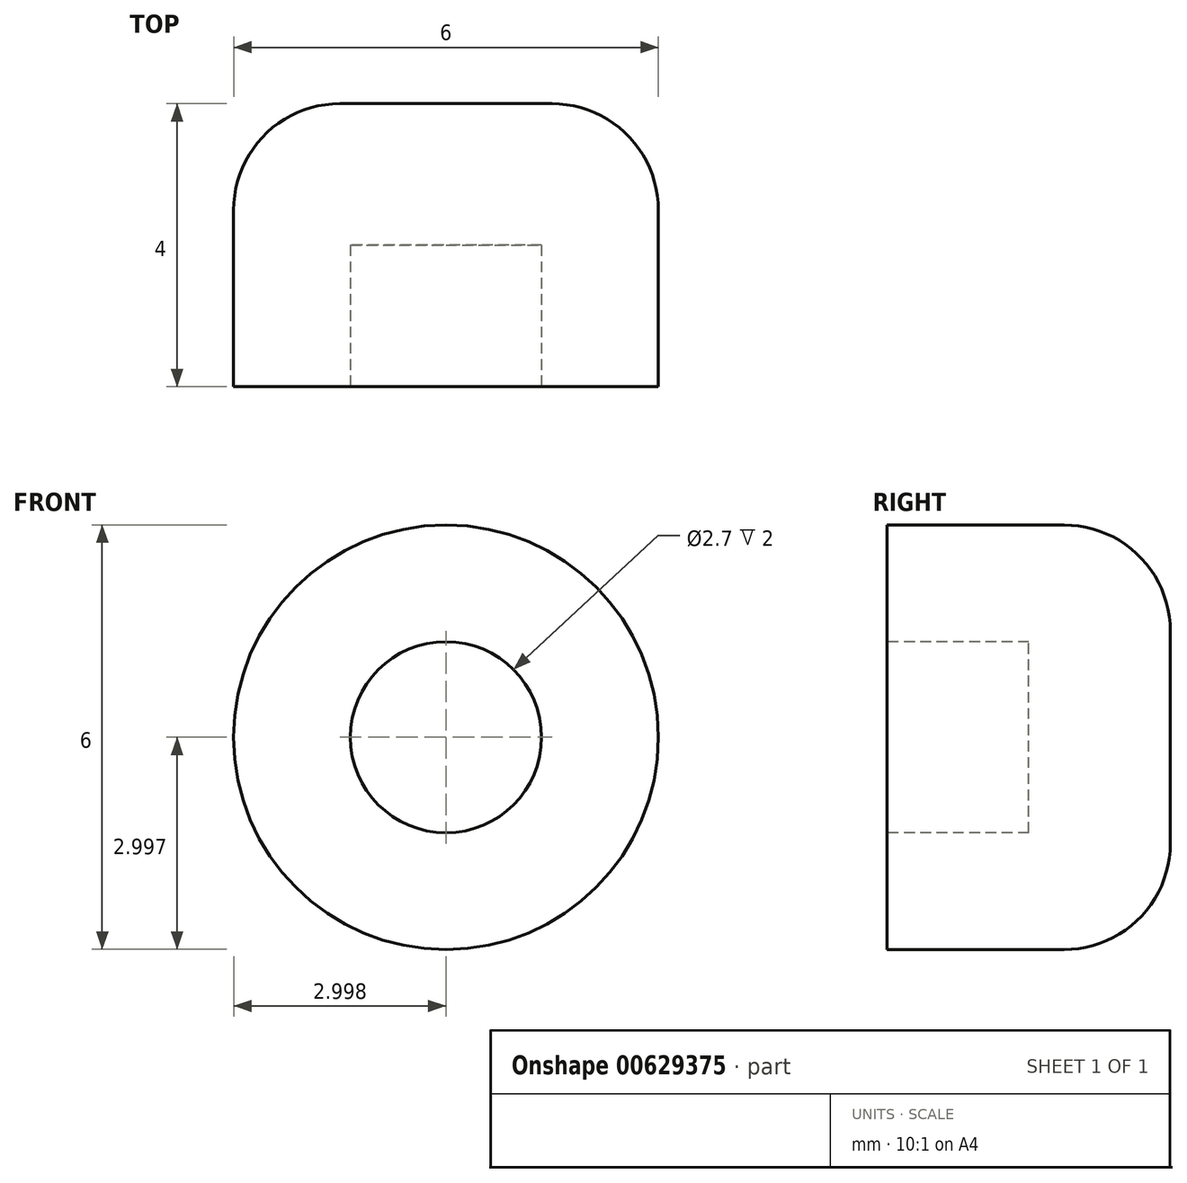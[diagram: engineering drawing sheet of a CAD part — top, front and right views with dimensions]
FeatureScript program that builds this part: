
annotation { "Feature Type Name" : "Feature", "Feature Type Description" : "" }
export const myFeature = defineFeature(function(context is Context, id is Id, definition is map)
    precondition{}
    {
        {
            var Q0;
            Q0=qCreatedBy(makeId("Front.planeOp"),FACE);
            var sketch = newSketch(context, id + "F0", { "sketchPlane" : qUnion([Q0])});
            skCircle(sketch, "E0", {"center": v(-17.47, 9.87) * mm, "radius": 3 * mm});
            skSolve(sketch);
        }
        {
            var Q0;
            Q0=makeQuery(id+"F0.imprint","IMPRINT",FACE,{"disambiguationData":[TD([[makeQuery(id+"F0.imprint","IMPRINT",EDGE,{"derivedFrom":sQuery(id+"F0.wireOp",EDGE,"E0")}),1.0]])]});
            extrude(context, id + "F1", {"entities" : qUnion([Q0]), "depth" : 4 * mm, "offsetDistance" : 25 * mm});
        }
        {
            var Q0;
            Q0=makeQuery(id+"F1.opExtrude","CAP_FACE",FACE,{"disambiguationData":[OSD([sQuery(id+"F0.wireOp",EDGE,"E0")])],"isStart":false});
            var sketch = newSketch(context, id + "F2", { "sketchPlane" : qUnion([Q0])});
            skCircle(sketch, "E1", {"center": v(-17.47, 9.87) * mm, "radius": 1.35 * mm});
            skSolve(sketch);
        }
        {
            var Q0;
            Q0=makeQuery(id+"F2.imprint","IMPRINT",FACE,{"disambiguationData":[TD([[makeQuery(id+"F2.imprint","IMPRINT",EDGE,{"derivedFrom":sQuery(id+"F2.wireOp",EDGE,"E1")}),1.0]])]});
            extrude(context, id + "F3", {"entities" : qUnion([Q0]), "operationType" : NewBodyOperationType.REMOVE, "oppositeDirection" : true, "depth" : 2 * mm, "offsetDistance" : 25 * mm});
        }
        {
            var Q0;
            Q0=makeQuery(id+"F1.opExtrude","CAP_EDGE",EDGE,{"disambiguationData":[OSD([sQuery(id+"F0.wireOp",EDGE,"E0")])],"isStart":true});
            fillet(context, id + "F4", {"entities" : qUnion([Q0]), "radius" : 1.5 * mm, "tangentPropagation" : true, "allowEdgeOverflow" : false});
        }
    });
